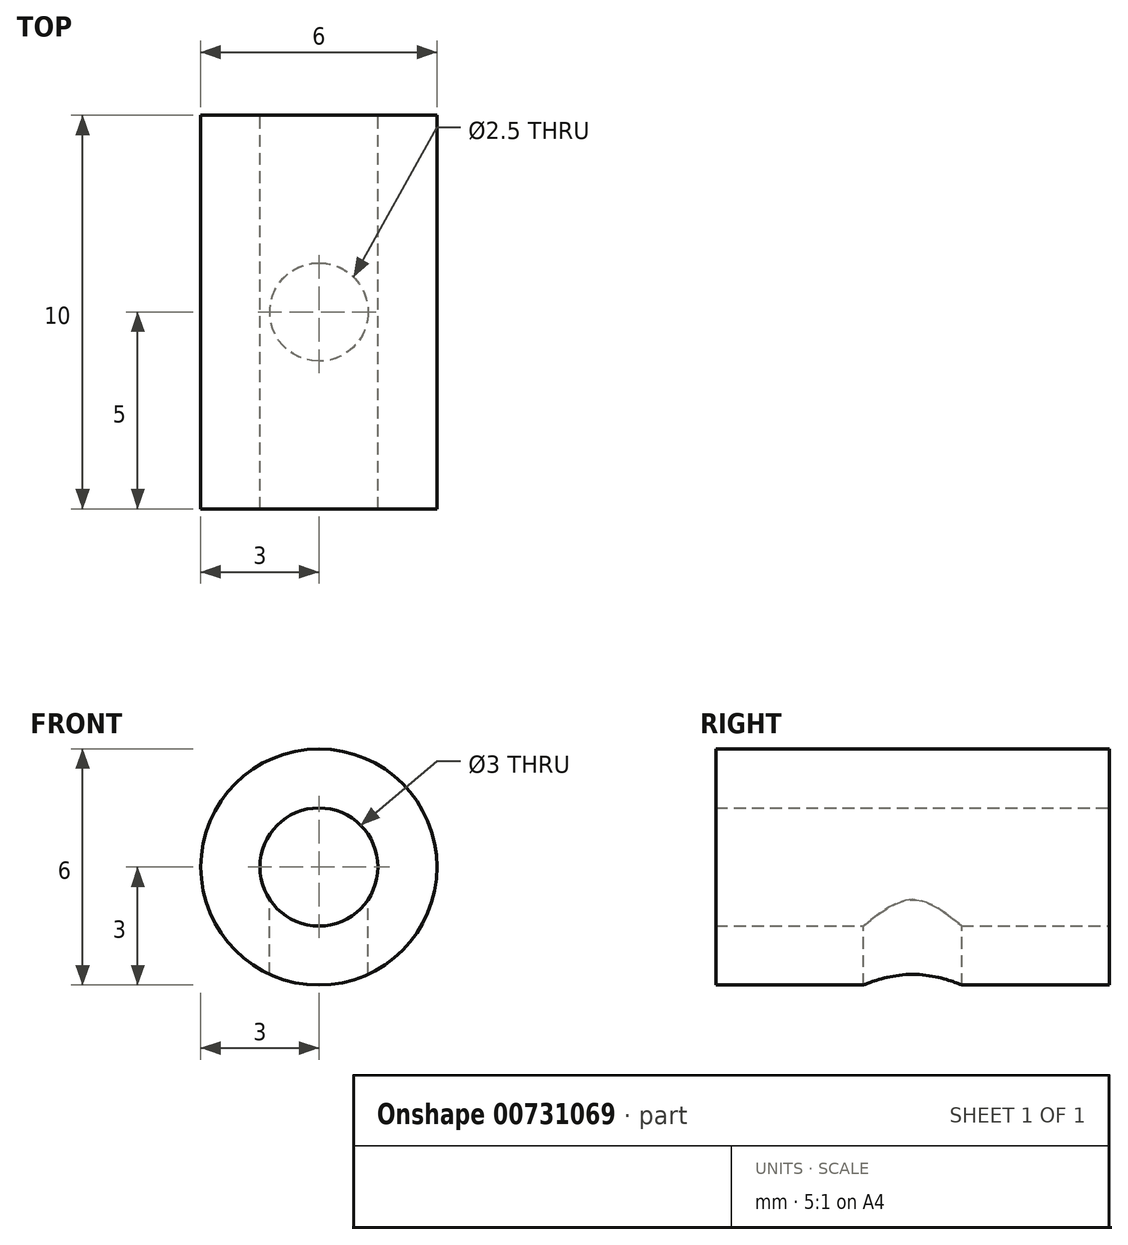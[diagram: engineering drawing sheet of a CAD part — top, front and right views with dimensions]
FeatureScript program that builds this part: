
annotation { "Feature Type Name" : "Feature", "Feature Type Description" : "" }
export const myFeature = defineFeature(function(context is Context, id is Id, definition is map)
    precondition{}
    {
        {
            var Q0;
            Q0=qCreatedBy(makeId("Front.planeOp"),FACE);
            var sketch = newSketch(context, id + "F0", { "sketchPlane" : qUnion([Q0])});
            skCircle(sketch, "E0", {"center": v(0, 0) * mm, "radius": 1.5 * mm});
            skCircle(sketch, "E1", {"center": v(0, 0) * mm, "radius": 3 * mm});
            skSolve(sketch);
        }
        {
            var Q0;
            Q0=makeQuery(id+"F0.imprint","IMPRINT",FACE,{"disambiguationData":[TD([[makeQuery(id+"F0.imprint","IMPRINT",EDGE,{"derivedFrom":sQuery(id+"F0.wireOp",EDGE,"E0")}),-1.0]])]});
            extrude(context, id + "F1", {"entities" : qUnion([Q0]), "depth" : 10 * mm, "offsetDistance" : 25 * mm});
        }
        {
            var Q0;
            Q0=qCreatedBy(makeId("Top.planeOp"),FACE);
            var sketch = newSketch(context, id + "F2", { "sketchPlane" : qUnion([Q0])});
            skPoint(sketch, "E2", {"position": v(0, -5) * mm});
            skSolve(sketch);
        }
        {
            var Q0;
            Q0=sQuery(id+"F2.wireOp",VERTEX,"E2");
            var Q1;
            Q1=makeQuery(id+"F1.opExtrude","SWEPT_BODY",BODY,{"disambiguationData":[OSD([sQuery(id+"F0.wireOp",EDGE,"E0"),sQuery(id+"F0.wireOp",EDGE,"E1")])]});
            hole(context, id + "F3", {"style" : HoleStyle.SIMPLE, "endStyle" : HoleEndStyle.BLIND, "standardTappedOrClearance" : lookupTablePath({ "fit" : "Normal", "standard" : "ISO", "engagement" : "75%", "pitch" : "0.5 mm", "size" : "M3", "type" : "Tapped" }), "standardBlindInLast" : lookupTablePath({ "fit" : "Standard", "standard" : "ISO", "engagement" : "75%", "pitch" : "0.5 mm", "size" : "M3", "type" : "Tapped" }), "holeDiameter" : 2.5 * mm, "majorDiameter" : 3 * mm, "showTappedDepth" : true, "holeDepth" : 4 * mm, "isTappedThrough" : true, "tappedDepth" : 2.5 * mm, "tapClearance" : 3, "startFromSketch" : true, "locations" : qUnion([Q0]), "scope" : qUnion([Q1])});
        }
    });
